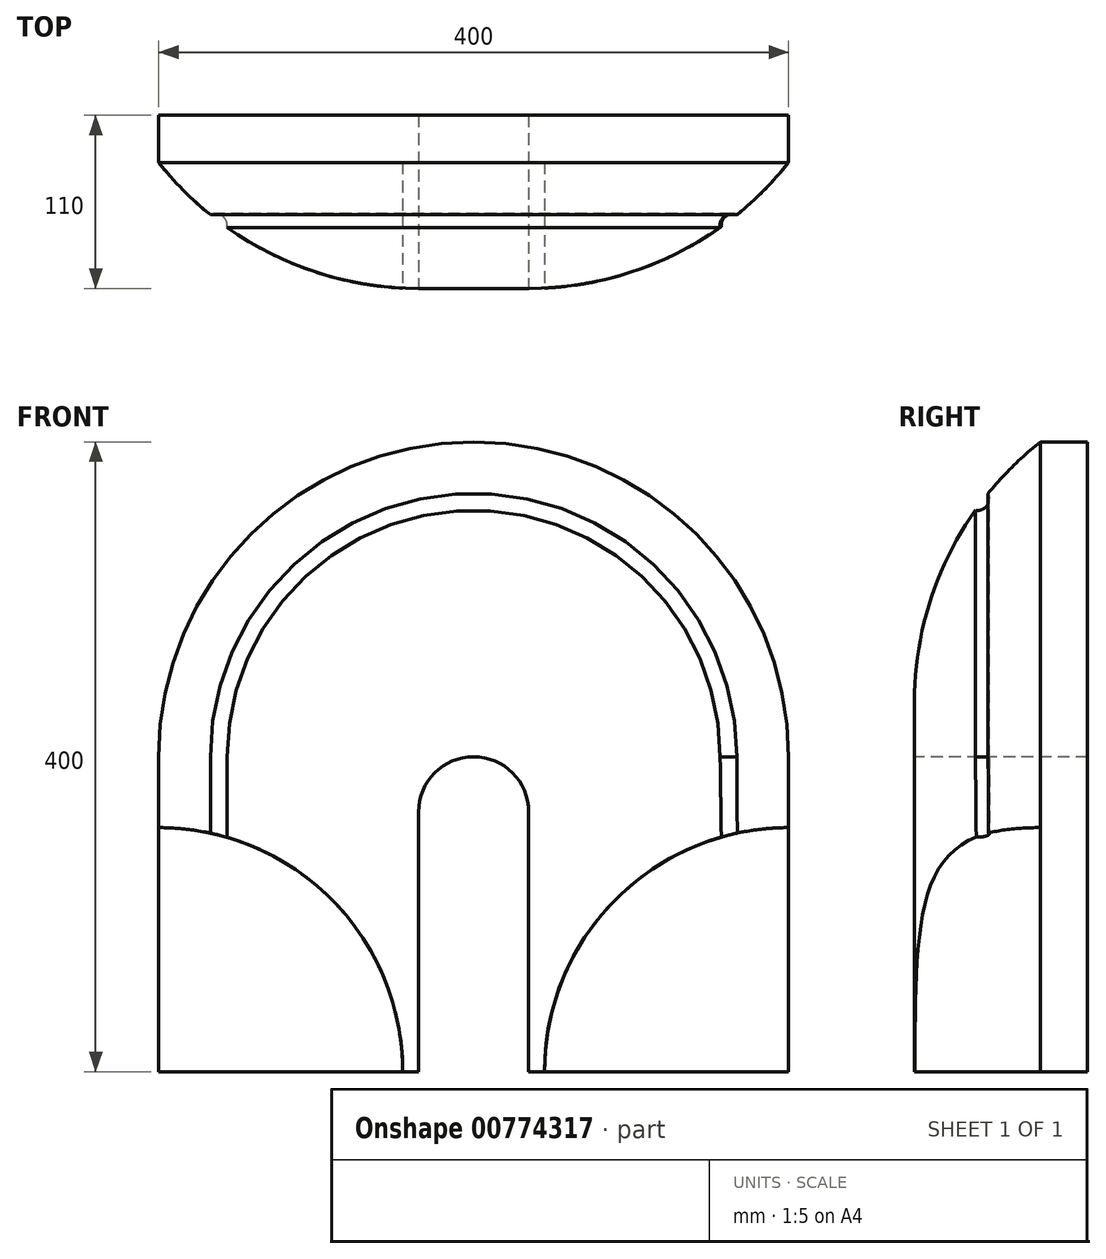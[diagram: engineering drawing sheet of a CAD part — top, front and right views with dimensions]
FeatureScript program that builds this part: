
annotation { "Feature Type Name" : "Feature", "Feature Type Description" : "" }
export const myFeature = defineFeature(function(context is Context, id is Id, definition is map)
    precondition{}
    {
        {
            var Q0;
            Q0=qCreatedBy(makeId("Front.planeOp"),FACE);
            var sketch = newSketch(context, id + "F0", { "sketchPlane" : qUnion([Q0])});
            skLineSegment(sketch, "E0.bottom", {"start": v(0, 0) * mm, "end": v(400, 0) * mm});
            skLineSegment(sketch, "E0.top", {"start": v(0, 200) * mm, "end": v(400, 200) * mm});
            skLineSegment(sketch, "E0.left", {"start": v(0, 0) * mm, "end": v(0, 200) * mm});
            skLineSegment(sketch, "E0.right", {"start": v(400, 0) * mm, "end": v(400, 200) * mm});
            skArc(sketch, "E1", {"start": v(400, 200) * mm, "mid": v(200, 400) * mm, "end": v(0, 200) * mm});
            skSolve(sketch);
        }
        {
            var Q0;
            Q0=makeQuery(id+"F0.imprint","IMPRINT",FACE,{"disambiguationData":[TD([[makeQuery(id+"F0.imprint","IMPRINT",EDGE,{"derivedFrom":sQuery(id+"F0.wireOp",EDGE,"E0.top")}),1.0]])]});
            var Q1;
            Q1=makeQuery(id+"F0.imprint","IMPRINT",FACE,{"disambiguationData":[TD([[makeQuery(id+"F0.imprint","IMPRINT",EDGE,{"derivedFrom":sQuery(id+"F0.wireOp",EDGE,"E0.bottom")}),1.0]])]});
            extrude(context, id + "F1", {"entities" : qUnion([Q0, Q1]), "depth" : 80 * mm, "offsetDistance" : 25 * mm});
        }
        {
            var Q0;
            Q0=makeQuery(id+"F1.opExtrude","CAP_EDGE",EDGE,{"disambiguationData":[OSD([sQuery(id+"F0.wireOp",EDGE,"E0.right")])],"isStart":false});
            var Q1;
            Q1=makeQuery(id+"F1.opExtrude","CAP_EDGE",EDGE,{"disambiguationData":[OSD([sQuery(id+"F0.wireOp",EDGE,"E0.left")])],"isStart":false});
            fillet(context, id + "F2", {"entities" : qUnion([Q0, Q1]), "radius" : 210 * mm, "tangentPropagation" : true, "allowEdgeOverflow" : false});
        }
        {
            var Q0;
            Q0=qCreatedBy(makeId("Front.planeOp"),FACE);
            cPlane(context, id + "F3", {"entities" : qUnion([Q0]), "cplaneType" : CPlaneType.OFFSET, "offset" : 80 * mm, "width" : 150 * mm, "height" : 150 * mm});
        }
        {
            var Q0;
            Q0=qCreatedBy(id+"F3.planeOp",FACE);
            var sketch = newSketch(context, id + "F4", { "sketchPlane" : qUnion([Q0])});
            skLineSegment(sketch, "E2.bottom", {"start": v(165, 0) * mm, "end": v(235, 0) * mm});
            skLineSegment(sketch, "E2.top", {"start": v(165, 165) * mm, "end": v(235, 165) * mm});
            skLineSegment(sketch, "E2.left", {"start": v(165, 0) * mm, "end": v(165, 165) * mm});
            skLineSegment(sketch, "E2.right", {"start": v(235, 0) * mm, "end": v(235, 165) * mm});
            skArc(sketch, "E3", {"start": v(235, 165) * mm, "mid": v(200, 200) * mm, "end": v(165, 165) * mm});
            skSolve(sketch);
        }
        {
            var Q0;
            Q0=makeQuery(id+"F4.imprint","IMPRINT",FACE,{"disambiguationData":[TD([[makeQuery(id+"F4.imprint","IMPRINT",EDGE,{"derivedFrom":sQuery(id+"F4.wireOp",EDGE,"E2.bottom")}),1.0]])]});
            var Q1;
            Q1=makeQuery(id+"F4.imprint","IMPRINT",FACE,{"disambiguationData":[TD([[makeQuery(id+"F4.imprint","IMPRINT",EDGE,{"derivedFrom":sQuery(id+"F4.wireOp",EDGE,"E2.top")}),1.0]])]});
            extrude(context, id + "F5", {"entities" : qUnion([Q0, Q1]), "operationType" : NewBodyOperationType.REMOVE, "oppositeDirection" : true, "depth" : 127 * mm, "offsetDistance" : 25 * mm});
        }
        {
            var Q0;
            Q0=qCreatedBy(id+"F3.planeOp",FACE);
            var sketch = newSketch(context, id + "F6", { "sketchPlane" : qUnion([Q0])});
            skCircle(sketch, "E4", {"center": v(0, 0) * mm, "radius": 155 * mm});
            skCircle(sketch, "E5", {"center": v(400, 0) * mm, "radius": 155 * mm});
            skSolve(sketch);
        }
        {
            var Q0;
            Q0=makeQuery(id+"F1.opExtrude","CAP_FACE",FACE,{"disambiguationData":[OSD([sQuery(id+"F0.wireOp",EDGE,"E0.bottom"),sQuery(id+"F0.wireOp",EDGE,"E0.left"),sQuery(id+"F0.wireOp",EDGE,"E0.right"),sQuery(id+"F0.wireOp",EDGE,"E1")])],"isStart":true});
            extrude(context, id + "F7", {"entities" : qUnion([Q0]), "operationType" : NewBodyOperationType.ADD, "depth" : 30 * mm, "offsetDistance" : 25 * mm});
        }
        {
            var Q0;
            Q0=makeQuery(id+"F6.imprint","IMPRINT",FACE,{"disambiguationData":[TD([[makeQuery(id+"F6.imprint","IMPRINT",EDGE,{"derivedFrom":sQuery(id+"F6.wireOp",EDGE,"E4")}),1.0]])]});
            var Q1;
            Q1=makeQuery(id+"F6.imprint","IMPRINT",FACE,{"disambiguationData":[TD([[makeQuery(id+"F6.imprint","IMPRINT",EDGE,{"derivedFrom":sQuery(id+"F6.wireOp",EDGE,"E5")}),1.0]])]});
            extrude(context, id + "F8", {"entities" : qUnion([Q0, Q1]), "operationType" : NewBodyOperationType.REMOVE, "oppositeDirection" : true, "depth" : 80 * mm, "offsetDistance" : 25 * mm});
        }
        {
            var Q0;
            Q0=qCreatedBy(makeId("Front.planeOp"),FACE);
            cPlane(context, id + "F9", {"entities" : qUnion([Q0]), "cplaneType" : CPlaneType.OFFSET, "offset" : 40 * mm, "width" : 150 * mm, "height" : 150 * mm});
        }
        {
            var Q0;
            Q0=qCreatedBy(id+"F9.planeOp",FACE);
            var sketch = newSketch(context, id + "F10", { "sketchPlane" : qUnion([Q0])});
            skPoint(sketch, "E6", {"position": v(36.02, 200) * mm});
            skPoint(sketch, "E7", {"position": v(363.98, 200) * mm});
            skLineSegment(sketch, "E8", {"start": v(36.02, 200) * mm, "end": v(36.02, 140) * mm});
            skLineSegment(sketch, "E9", {"start": v(363.98, 200) * mm, "end": v(364.89, 140) * mm});
            skArc(sketch, "E10", {"start": v(363.98, 200) * mm, "mid": v(200, 363.98) * mm, "end": v(36.02, 200) * mm});
            skSolve(sketch);
        }
        {
            var Q0;
            Q0=qCreatedBy(makeId("Top.planeOp"),FACE);
            cPlane(context, id + "F11", {"entities" : qUnion([Q0]), "cplaneType" : CPlaneType.OFFSET, "offset" : 200 * mm, "width" : 150 * mm, "height" : 150 * mm});
        }
        {
            var Q0;
            Q0=qCreatedBy(id+"F11.planeOp",FACE);
            var sketch = newSketch(context, id + "F12", { "sketchPlane" : qUnion([Q0])});
            skCircle(sketch, "E11", {"center": v(36.02, -40) * mm, "radius": 7.5 * mm});
            skSolve(sketch);
        }
        {
            var Q0;
            Q0=makeQuery(id+"F12.imprint","IMPRINT",FACE,{"disambiguationData":[TD([[makeQuery(id+"F12.imprint","IMPRINT",EDGE,{"derivedFrom":sQuery(id+"F12.wireOp",EDGE,"E11")}),1.0]])]});
            var Q1;
            Q1=sQuery(id+"F10.wireOp",EDGE,"E8");
            var Q2;
            Q2=sQuery(id+"F10.wireOp",EDGE,"E10");
            var Q3;
            Q3=sQuery(id+"F10.wireOp",EDGE,"E9");
            sweep(context, id + "F13", {"operationType" : NewBodyOperationType.REMOVE, "profiles" : qUnion([Q0]), "path" : qUnion([Q1, Q2, Q3])});
        }
    });
